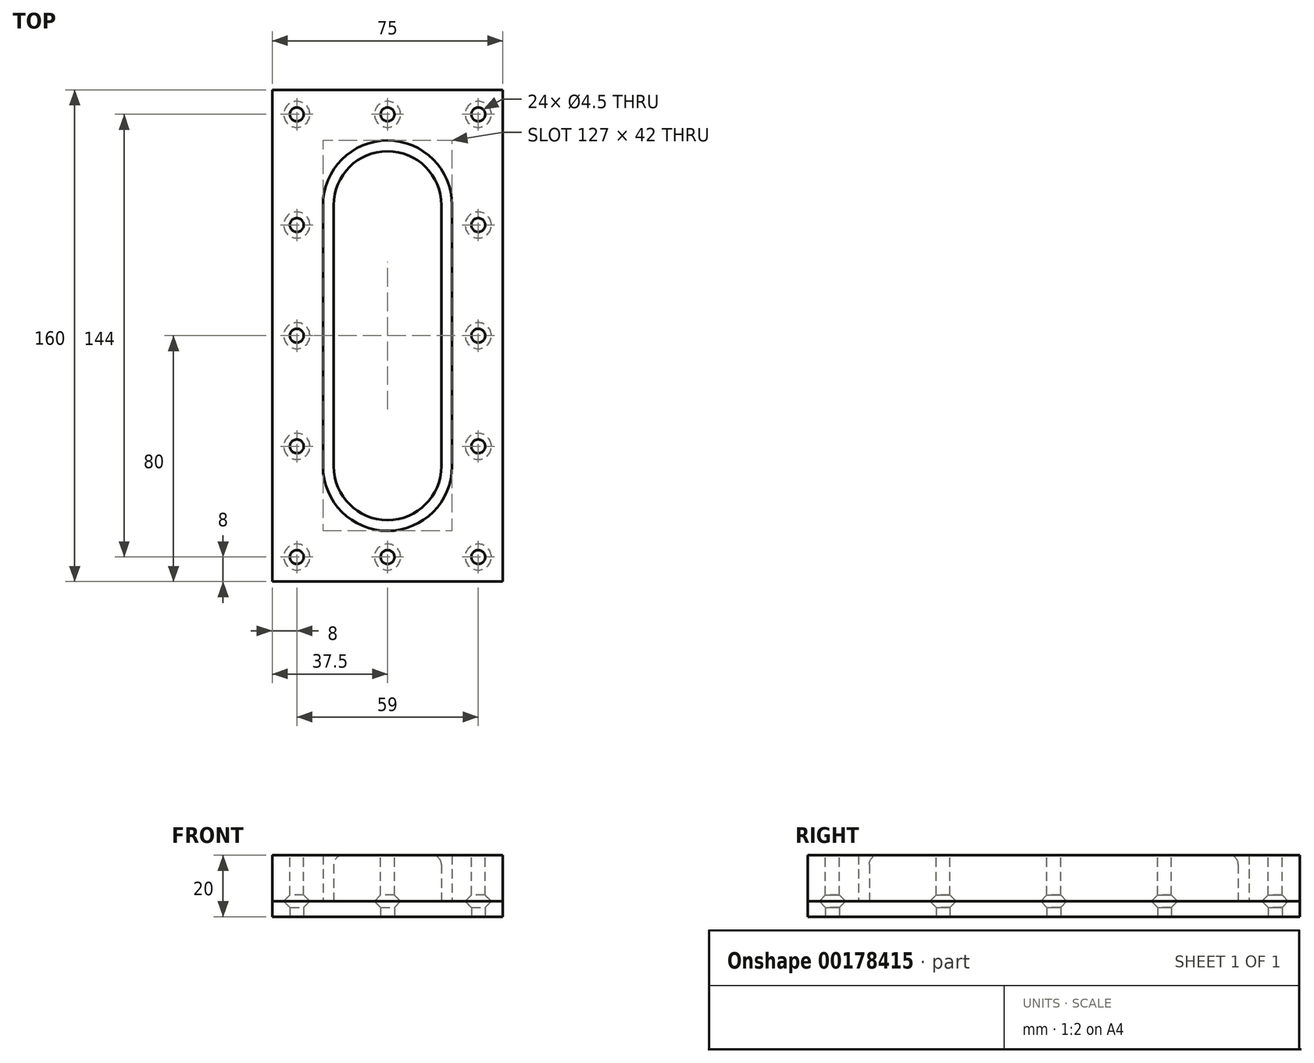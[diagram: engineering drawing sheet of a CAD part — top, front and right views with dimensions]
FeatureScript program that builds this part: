
annotation { "Feature Type Name" : "Feature", "Feature Type Description" : "" }
export const myFeature = defineFeature(function(context is Context, id is Id, definition is map)
    precondition{}
    {
        {
            var Q0;
            Q0=qCreatedBy(makeId("Top.planeOp"),FACE);
            var sketch = newSketch(context, id + "F0", { "sketchPlane" : qUnion([Q0])});
            skLineSegment(sketch, "E0.bottom", {"start": v(37.5, 80) * mm, "end": v(-37.5, 80) * mm});
            skLineSegment(sketch, "E0.top", {"start": v(37.5, -80) * mm, "end": v(-37.5, -80) * mm});
            skLineSegment(sketch, "E0.left", {"start": v(37.5, 80) * mm, "end": v(37.5, -80) * mm});
            skLineSegment(sketch, "E0.right", {"start": v(-37.5, 80) * mm, "end": v(-37.5, -80) * mm});
            skPoint(sketch, "E0.middle", {"position": v(0, 0) * mm});
            skLineSegment(sketch, "E1", {"start": v(-17.5, 42.5) * mm, "end": v(-17.5, -42.5) * mm});
            skLineSegment(sketch, "E2", {"start": v(17.5, 42.5) * mm, "end": v(17.5, -42.5) * mm});
            skArc(sketch, "E3", {"start": v(-17.5, 42.5) * mm, "mid": v(0, 60) * mm, "end": v(17.5, 42.5) * mm});
            skArc(sketch, "E4", {"start": v(-17.5, -42.5) * mm, "mid": v(0, -60) * mm, "end": v(17.5, -42.5) * mm});
            skPoint(sketch, "E5", {"position": v(-29.5, 72) * mm});
            skPoint(sketch, "E6.0.1.0", {"position": v(-29.5, 36) * mm});
            skPoint(sketch, "E6.0.2.0", {"position": v(-29.5, 0) * mm});
            skPoint(sketch, "E6.0.3.0", {"position": v(-29.5, -36) * mm});
            skPoint(sketch, "E6.0.4.0", {"position": v(-29.5, -72) * mm});
            skLineSegment(sketch, "E6.direction1", {"start": v(-75, 72) * mm, "end": v(-29.5, 72) * mm, "construction": true});
            skLineSegment(sketch, "E6.direction2", {"start": v(-29.5, 72) * mm, "end": v(-29.5, 36) * mm, "construction": true});
            skPoint(sketch, "E7", {"position": v(0, 72) * mm});
            skPoint(sketch, "E8", {"position": v(0, -72) * mm});
            skLineSegment(sketch, "E9", {"start": v(0, 42.5) * mm, "end": v(0, -42.5) * mm, "construction": true});
            skPoint(sketch, "E10.MirrorP", {"position": v(29.5, 72) * mm});
            skPoint(sketch, "E11.MirrorP", {"position": v(29.5, 36) * mm});
            skPoint(sketch, "E12.MirrorP", {"position": v(29.5, 0) * mm});
            skPoint(sketch, "E13.MirrorP", {"position": v(29.5, -36) * mm});
            skPoint(sketch, "E14.MirrorP", {"position": v(29.5, -72) * mm});
            skLineSegment(sketch, "E15.0", {"start": v(21, 42.5) * mm, "end": v(21, -42.5) * mm});
            skArc(sketch, "E15.1", {"start": v(-21, 42.5) * mm, "mid": v(0, 63.5) * mm, "end": v(21, 42.5) * mm});
            skLineSegment(sketch, "E15.2", {"start": v(-21, 42.5) * mm, "end": v(-21, -42.5) * mm});
            skArc(sketch, "E15.3", {"start": v(-21, -42.5) * mm, "mid": v(0, -63.5) * mm, "end": v(21, -42.5) * mm});
            skSolve(sketch);
        }
        {
            var Q0;
            Q0=makeQuery(id+"F0.imprint","IMPRINT",FACE,{"disambiguationData":[TD([[makeQuery(id+"F0.imprint","IMPRINT",EDGE,{"derivedFrom":sQuery(id+"F0.wireOp",EDGE,"E0.bottom")}),1.0]])]});
            var Q1;
            Q1=makeQuery(id+"F0.imprint","IMPRINT",FACE,{"disambiguationData":[TD([[makeQuery(id+"F0.imprint","IMPRINT",EDGE,{"derivedFrom":sQuery(id+"F0.wireOp",EDGE,"E1")}),1.0]])]});
            var Q2;
            Q2=makeQuery(id+"F0.imprint","IMPRINT",FACE,{"disambiguationData":[TD([[makeQuery(id+"F0.imprint","IMPRINT",EDGE,{"derivedFrom":sQuery(id+"F0.wireOp",EDGE,"E1")}),-1.0]])]});
            extrude(context, id + "F1", {"entities" : qUnion([Q0, Q1, Q2]), "oppositeDirection" : true, "depth" : 5 * mm});
        }
        {
            var Q0;
            Q0=makeQuery(id+"F0.imprint","IMPRINT",FACE,{"disambiguationData":[TD([[makeQuery(id+"F0.imprint","IMPRINT",EDGE,{"derivedFrom":sQuery(id+"F0.wireOp",EDGE,"E1")}),1.0]])]});
            extrude(context, id + "F2", {"entities" : qUnion([Q0]), "operationType" : NewBodyOperationType.ADD, "depth" : 15 * mm});
        }
        {
            var Q0;
            Q0=makeQuery(id+"F0.imprint","IMPRINT",FACE,{"disambiguationData":[TD([[makeQuery(id+"F0.imprint","IMPRINT",EDGE,{"derivedFrom":sQuery(id+"F0.wireOp",EDGE,"E0.bottom")}),1.0]])]});
            var Q1;
            Q1=makeQuery(id+"F2.opExtrude","CAP_FACE",FACE,{"disambiguationData":[OSD([sQuery(id+"F0.wireOp",EDGE,"E1"),sQuery(id+"F0.wireOp",EDGE,"E2"),sQuery(id+"F0.wireOp",EDGE,"E3"),sQuery(id+"F0.wireOp",EDGE,"E4")])],"isStart":false});
            extrude(context, id + "F3", {"entities" : qUnion([Q0]), "endBound" : BoundingType.UP_TO_SURFACE, "endBoundEntityFace" : qUnion([Q1]), "depth" : 25 * mm});
        }
        {
            var Q0;
            Q0=sQuery(id+"F0.wireOp",VERTEX,"E5");
            var Q1;
            Q1=sQuery(id+"F0.wireOp",VERTEX,"E6.0.1.0");
            var Q2;
            Q2=sQuery(id+"F0.wireOp",VERTEX,"E6.0.2.0");
            var Q3;
            Q3=sQuery(id+"F0.wireOp",VERTEX,"E6.0.3.0");
            var Q4;
            Q4=sQuery(id+"F0.wireOp",VERTEX,"E6.0.4.0");
            var Q5;
            Q5=sQuery(id+"F0.wireOp",VERTEX,"E8");
            var Q6;
            Q6=sQuery(id+"F0.wireOp",VERTEX,"E14.MirrorP");
            var Q7;
            Q7=sQuery(id+"F0.wireOp",VERTEX,"E13.MirrorP");
            var Q8;
            Q8=sQuery(id+"F0.wireOp",VERTEX,"E12.MirrorP");
            var Q9;
            Q9=sQuery(id+"F0.wireOp",VERTEX,"E11.MirrorP");
            var Q10;
            Q10=sQuery(id+"F0.wireOp",VERTEX,"E10.MirrorP");
            var Q11;
            Q11=sQuery(id+"F0.wireOp",VERTEX,"E7");
            var Q12;
            Q12=makeQuery(id+"F1.opExtrude","SWEPT_BODY",BODY,{"disambiguationData":[OSD([sQuery(id+"F0.wireOp",EDGE,"E0.bottom"),sQuery(id+"F0.wireOp",EDGE,"E0.top"),sQuery(id+"F0.wireOp",EDGE,"E0.left"),sQuery(id+"F0.wireOp",EDGE,"E0.right")])]});
            hole(context, id + "F4", {"style" : HoleStyle.C_SINK, "endStyle" : HoleEndStyle.THROUGH, "holeDiameter" : 4.5 * mm, "cSinkDiameter" : 8.5 * mm, "cSinkAngle" : 90 * degree, "locations" : qUnion([Q0, Q1, Q2, Q3, Q4, Q5, Q6, Q7, Q8, Q9, Q10, Q11]), "scope" : qUnion([Q12]), "isTappedThrough" : true, "startStyle" : HoleStartStyle.PART});
        }
        {
            var Q0;
            Q0=sQuery(id+"F0.wireOp",VERTEX,"E5");
            var Q1;
            Q1=sQuery(id+"F0.wireOp",VERTEX,"E6.0.1.0");
            var Q2;
            Q2=sQuery(id+"F0.wireOp",VERTEX,"E6.0.2.0");
            var Q3;
            Q3=sQuery(id+"F0.wireOp",VERTEX,"E6.0.3.0");
            var Q4;
            Q4=sQuery(id+"F0.wireOp",VERTEX,"E6.0.4.0");
            var Q5;
            Q5=sQuery(id+"F0.wireOp",VERTEX,"E8");
            var Q6;
            Q6=sQuery(id+"F0.wireOp",VERTEX,"E14.MirrorP");
            var Q7;
            Q7=sQuery(id+"F0.wireOp",VERTEX,"E13.MirrorP");
            var Q8;
            Q8=sQuery(id+"F0.wireOp",VERTEX,"E12.MirrorP");
            var Q9;
            Q9=sQuery(id+"F0.wireOp",VERTEX,"E11.MirrorP");
            var Q10;
            Q10=sQuery(id+"F0.wireOp",VERTEX,"E10.MirrorP");
            var Q11;
            Q11=sQuery(id+"F0.wireOp",VERTEX,"E7");
            var Q12;
            Q12=makeQuery(id+"F3.opExtrude","SWEPT_BODY",BODY,{"disambiguationData":[OSD([sQuery(id+"F0.wireOp",EDGE,"E0.bottom"),sQuery(id+"F0.wireOp",EDGE,"E0.top"),sQuery(id+"F0.wireOp",EDGE,"E0.left"),sQuery(id+"F0.wireOp",EDGE,"E0.right"),sQuery(id+"F0.wireOp",EDGE,"E15.0"),sQuery(id+"F0.wireOp",EDGE,"E15.1"),sQuery(id+"F0.wireOp",EDGE,"E15.2"),sQuery(id+"F0.wireOp",EDGE,"E15.3")])]});
            hole(context, id + "F5", {"style" : HoleStyle.C_SINK, "endStyle" : HoleEndStyle.THROUGH, "oppositeDirection" : true, "holeDiameter" : 4.5 * mm, "cSinkDiameter" : 8.5 * mm, "cSinkAngle" : 90 * degree, "locations" : qUnion([Q0, Q1, Q2, Q3, Q4, Q5, Q6, Q7, Q8, Q9, Q10, Q11]), "scope" : qUnion([Q12]), "isTappedThrough" : true, "startStyle" : HoleStartStyle.PART});
        }
        {
            var Q0;
            Q0=makeQuery(id+"F2.opExtrude","CAP_EDGE",EDGE,{"disambiguationData":[OSD([sQuery(id+"F0.wireOp",EDGE,"E2")])],"isStart":false});
            fillet(context, id + "F6", {"entities" : qUnion([Q0]), "radius" : 3 * mm, "tangentPropagation" : true, "allowEdgeOverflow" : false});
        }
    });
